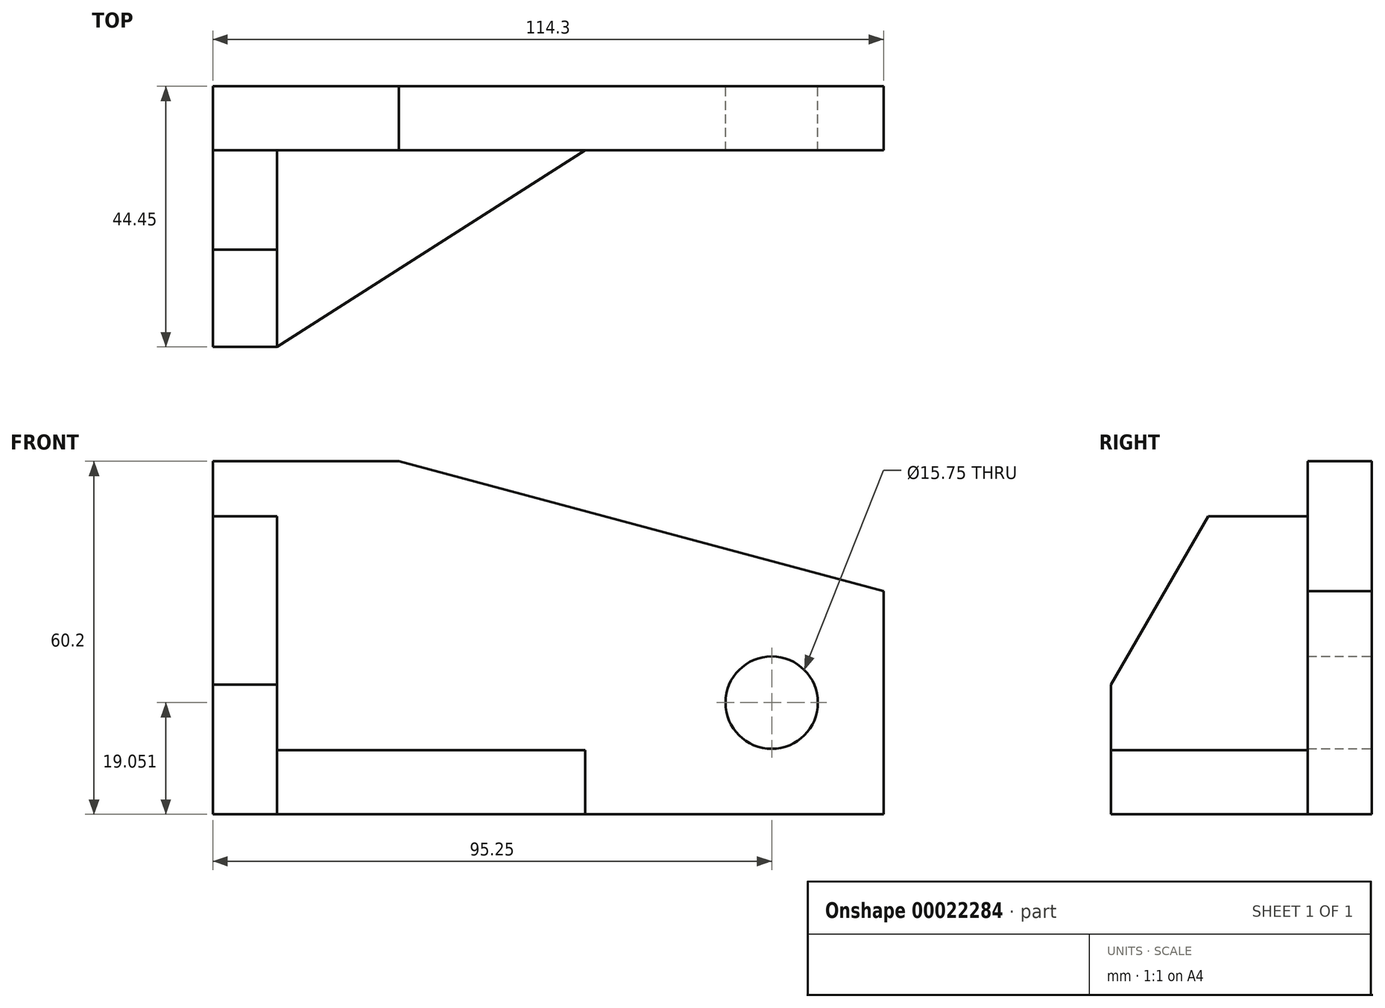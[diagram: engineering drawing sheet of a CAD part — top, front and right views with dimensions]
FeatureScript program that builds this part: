
annotation { "Feature Type Name" : "Feature", "Feature Type Description" : "" }
export const myFeature = defineFeature(function(context is Context, id is Id, definition is map)
    precondition{}
    {
        {
            var Q0;
            Q0=qCreatedBy(makeId("Front.planeOp"),FACE);
            var sketch = newSketch(context, id + "F0", { "sketchPlane" : qUnion([Q0])});
            skLineSegment(sketch, "E0.rect.bottom", {"start": v(57.15, 30.1) * mm, "end": v(-57.15, 30.1) * mm});
            skLineSegment(sketch, "E0.rect.top", {"start": v(57.15, -30.1) * mm, "end": v(-57.15, -30.1) * mm});
            skLineSegment(sketch, "E0.rect.left", {"start": v(57.15, 30.1) * mm, "end": v(57.15, -30.1) * mm});
            skLineSegment(sketch, "E0.rect.right", {"start": v(-57.15, 30.1) * mm, "end": v(-57.15, -30.1) * mm});
            skPoint(sketch, "E0.rect.middle", {"position": v(0, 0) * mm});
            skLineSegment(sketch, "E1", {"start": v(-25.4, 30.1) * mm, "end": v(57.15, 7.98) * mm});
            skCircle(sketch, "E2", {"center": v(38.1, -11.05) * mm, "radius": 7.87 * mm});
            skLineSegment(sketch, "E3.bottom", {"start": v(-57.15, 30.1) * mm, "end": v(-25.4, 30.1) * mm});
            skLineSegment(sketch, "E3.top", {"start": v(-57.15, -30.1) * mm, "end": v(-57.15, -30.1) * mm});
            skSolve(sketch);
        }
        {
            var Q0;
            {var subQ3=sQuery(id+"F0.wireOp",EDGE,"E0.rect.top");Q0=makeQuery(id+"F0.imprint","IMPRINT",FACE,{"disambiguationData":[TD([[makeQuery(id+"F0.imprint","IMPRINT",EDGE,{"derivedFrom":subQ3}),-1.0]])]});}
            extrude(context, id + "F1", {"entities" : qUnion([Q0]), "depth" : 10.92 * mm});
        }
        {
            var Q0;
            Q0=makeQuery(id+"F1.opExtrude","SWEPT_FACE",FACE,{"disambiguationData":[OSD([sQuery(id+"F0.wireOp",EDGE,"E0.rect.right")])]});
            var sketch = newSketch(context, id + "F2", { "sketchPlane" : qUnion([Q0])});
            skLineSegment(sketch, "E4.bottom", {"start": v(0, 20.7) * mm, "end": v(-44.45, 20.7) * mm});
            skLineSegment(sketch, "E4.top", {"start": v(0, -30.1) * mm, "end": v(-44.45, -30.1) * mm});
            skLineSegment(sketch, "E4.left", {"start": v(0, 20.7) * mm, "end": v(0, -30.1) * mm});
            skLineSegment(sketch, "E4.right", {"start": v(-44.45, 20.7) * mm, "end": v(-44.45, -30.1) * mm});
            skLineSegment(sketch, "E5", {"start": v(-27.88, 20.7) * mm, "end": v(-44.45, -8) * mm});
            skLineSegment(sketch, "E6.MirrorCS", {"start": v(27.88, 20.7) * mm, "end": v(44.45, -8) * mm});
            skLineSegment(sketch, "E7.MirrorCS", {"start": v(0, 20.7) * mm, "end": v(44.45, 20.7) * mm});
            skLineSegment(sketch, "E8.MirrorCS", {"start": v(44.45, 20.7) * mm, "end": v(44.45, -30.1) * mm});
            skLineSegment(sketch, "E9.MirrorCS", {"start": v(0, -30.1) * mm, "end": v(44.45, -30.1) * mm});
            skSolve(sketch);
        }
        {
            var Q0;
            {var subQ7=sQuery(id+"F2.wireOp",EDGE,"E6.MirrorCS");Q0=makeQuery(id+"F2.imprint","IMPRINT",FACE,{"disambiguationData":[TD([[makeQuery(id+"F2.imprint","IMPRINT",EDGE,{"derivedFrom":subQ7}),-1.0]])]});}
            extrude(context, id + "F3", {"entities" : qUnion([Q0]), "oppositeDirection" : true, "depth" : 10.92 * mm});
        }
        {
            var Q0;
            Q0=makeQuery(id+"F1.opExtrude","SWEPT_FACE",FACE,{"disambiguationData":[OSD([sQuery(id+"F0.wireOp",EDGE,"E0.rect.top")])]});
            var sketch = newSketch(context, id + "F4", { "sketchPlane" : qUnion([Q0])});
            skLineSegment(sketch, "E10.bottom", {"start": v(-57.15, 0) * mm, "end": v(6.35, 0) * mm});
            skLineSegment(sketch, "E10.top", {"start": v(-57.15, 44.45) * mm, "end": v(6.35, 44.45) * mm});
            skLineSegment(sketch, "E10.left", {"start": v(-57.15, 0) * mm, "end": v(-57.15, 44.45) * mm});
            skLineSegment(sketch, "E10.right", {"start": v(6.35, 0) * mm, "end": v(6.35, 44.45) * mm});
            skLineSegment(sketch, "E11", {"start": v(6.35, 10.92) * mm, "end": v(-46.23, 44.45) * mm});
            skSolve(sketch);
        }
        {
            var Q0;
            {var subQ1=sQuery(id+"F4.wireOp",EDGE,"E11");Q0=makeQuery(id+"F4.imprint","IMPRINT",FACE,{"disambiguationData":[TD([[makeQuery(id+"F4.imprint","IMPRINT",EDGE,{"derivedFrom":subQ1}),1.0]])]});}
            extrude(context, id + "F5", {"entities" : qUnion([Q0]), "operationType" : NewBodyOperationType.ADD, "oppositeDirection" : true, "depth" : 10.92 * mm});
        }
    });
